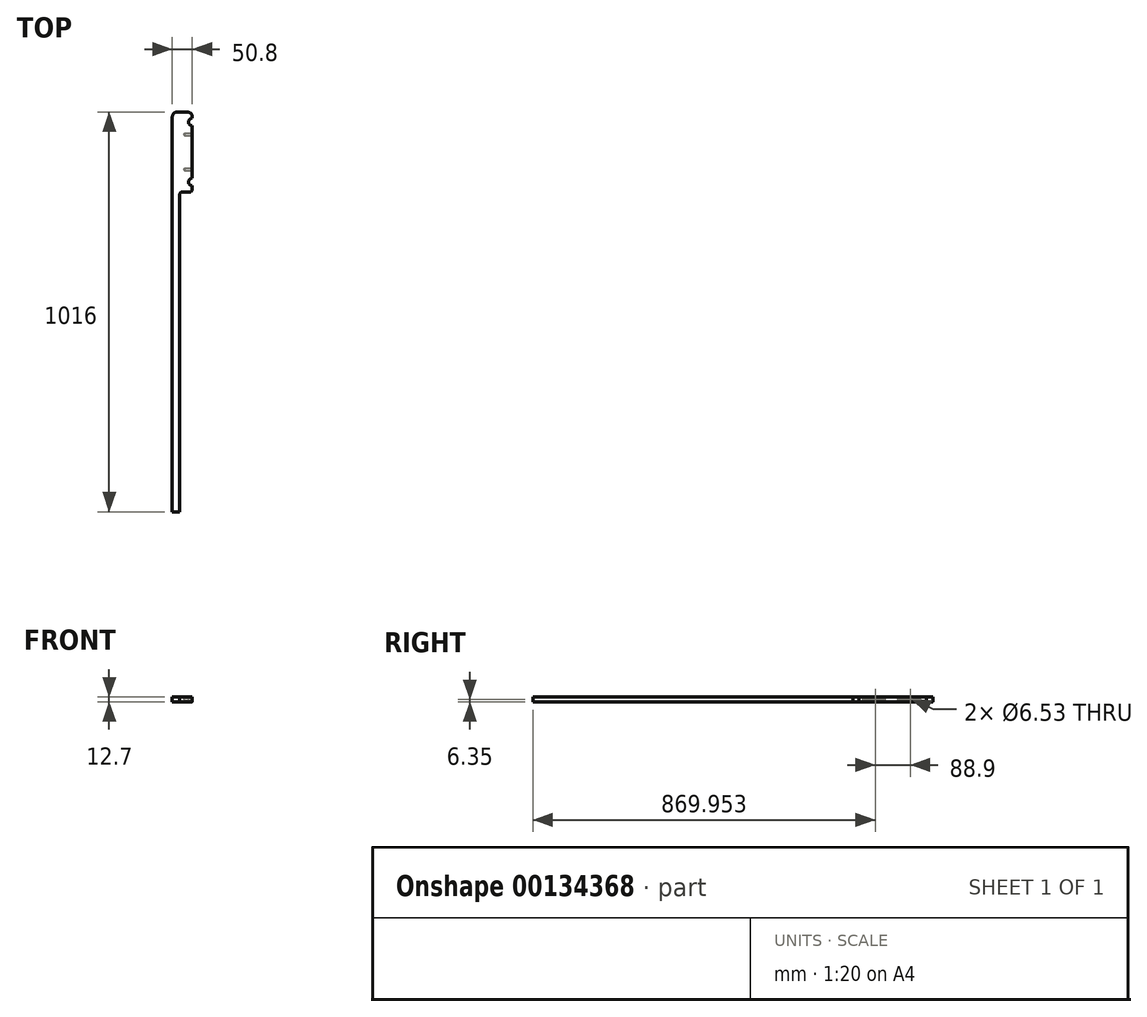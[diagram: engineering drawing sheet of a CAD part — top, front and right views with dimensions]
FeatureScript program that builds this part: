
annotation { "Feature Type Name" : "Feature", "Feature Type Description" : "" }
export const myFeature = defineFeature(function(context is Context, id is Id, definition is map)
    precondition{}
    {
        {
            var Q0;
            Q0=qCreatedBy(makeId("Top.planeOp"),FACE);
            var sketch = newSketch(context, id + "F0", { "sketchPlane" : qUnion([Q0])});
            skLineSegment(sketch, "E0", {"start": v(12.7, 1073.25) * mm, "end": v(38.1, 1073.25) * mm});
            skLineSegment(sketch, "E1", {"start": v(50.8, 1060.55) * mm, "end": v(50.8, 876.4) * mm});
            skLineSegment(sketch, "E2", {"start": v(44.45, 870.05) * mm, "end": v(25.4, 870.05) * mm});
            skLineSegment(sketch, "E3", {"start": v(0, 1060.55) * mm, "end": v(0, 57.25) * mm});
            skLineSegment(sketch, "E4", {"start": v(19.05, 863.7) * mm, "end": v(19.05, 57.25) * mm});
            skLineSegment(sketch, "E5", {"start": v(0, 57.25) * mm, "end": v(19.05, 57.25) * mm});
            skPoint(sketch, "E6.visualSharp", {"position": v(0, 1073.25) * mm});
            skArc(sketch, "E6.filletArc", {"start": v(12.7, 1073.25) * mm, "mid": v(3.72, 1069.53) * mm, "end": v(0, 1060.55) * mm});
            skPoint(sketch, "E7.visualSharp", {"position": v(50.8, 1073.25) * mm});
            skArc(sketch, "E7.filletArc", {"start": v(50.8, 1060.55) * mm, "mid": v(47.08, 1069.53) * mm, "end": v(38.1, 1073.25) * mm});
            skPoint(sketch, "E8.visualSharp", {"position": v(50.8, 870.05) * mm});
            skArc(sketch, "E8.filletArc", {"start": v(44.45, 870.05) * mm, "mid": v(48.94, 871.91) * mm, "end": v(50.8, 876.4) * mm});
            skPoint(sketch, "E9.visualSharp", {"position": v(19.05, 870.05) * mm});
            skArc(sketch, "E9.filletArc", {"start": v(25.4, 870.05) * mm, "mid": v(20.9, 868.2) * mm, "end": v(19.05, 863.7) * mm});
            skSolve(sketch);
        }
        {
            var Q0;
            Q0=makeQuery(id+"F0.imprint","IMPRINT",FACE,{"disambiguationData":[TD([[makeQuery(id+"F0.imprint","IMPRINT",EDGE,{"derivedFrom":sQuery(id+"F0.wireOp",EDGE,"E0")}),-1.0]])]});
            extrude(context, id + "F1", {"entities" : qUnion([Q0]), "depth" : 12.7 * mm});
        }
        {
            var Q0;
            Q0=makeQuery(id+"F1.opExtrude","CAP_FACE",FACE,{"disambiguationData":[OSD([sQuery(id+"F0.wireOp",EDGE,"E0"),sQuery(id+"F0.wireOp",EDGE,"E1"),sQuery(id+"F0.wireOp",EDGE,"E2"),sQuery(id+"F0.wireOp",EDGE,"E3"),sQuery(id+"F0.wireOp",EDGE,"E4"),sQuery(id+"F0.wireOp",EDGE,"E5"),sQuery(id+"F0.wireOp",EDGE,"E6.filletArc"),sQuery(id+"F0.wireOp",EDGE,"E7.filletArc"),sQuery(id+"F0.wireOp",EDGE,"E8.filletArc"),sQuery(id+"F0.wireOp",EDGE,"E9.filletArc")])],"isStart":false});
            var sketch = newSketch(context, id + "F2", { "sketchPlane" : qUnion([Q0])});
            skPoint(sketch, "E10", {"position": v(50.8, 1047.85) * mm});
            skPoint(sketch, "E11", {"position": v(50.8, 895.45) * mm});
            skSolve(sketch);
        }
        {
            var Q0;
            Q0=sQuery(id+"F2.wireOp",VERTEX,"E10");
            var Q1;
            Q1=sQuery(id+"F2.wireOp",VERTEX,"E11");
            var Q2;
            Q2=makeQuery(id+"F1.opExtrude","SWEPT_BODY",BODY,{"disambiguationData":[OSD([sQuery(id+"F0.wireOp",EDGE,"E0"),sQuery(id+"F0.wireOp",EDGE,"E1"),sQuery(id+"F0.wireOp",EDGE,"E2"),sQuery(id+"F0.wireOp",EDGE,"E3"),sQuery(id+"F0.wireOp",EDGE,"E4"),sQuery(id+"F0.wireOp",EDGE,"E5"),sQuery(id+"F0.wireOp",EDGE,"E6.filletArc"),sQuery(id+"F0.wireOp",EDGE,"E7.filletArc"),sQuery(id+"F0.wireOp",EDGE,"E8.filletArc"),sQuery(id+"F0.wireOp",EDGE,"E9.filletArc")])]});
            hole(context, id + "F3", {"style" : HoleStyle.SIMPLE, "endStyle" : HoleEndStyle.THROUGH, "holeDiameter" : 19.05 * mm, "locations" : qUnion([Q0, Q1]), "scope" : qUnion([Q2]), "isTappedThrough" : true});
        }
        {
            var Q0;
            {var subQ1=sQuery(id+"F0.wireOp",EDGE,"E8.filletArc");var subQ8=sQuery(id+"F0.wireOp",EDGE,"E1");var subQ12=makeQuery(id+"F3.hole-0.opRevolve","SWEPT_FACE",FACE,{"disambiguationData":[OSD([sQuery(id+"F3.hole-0.sketch.wireOp",EDGE,"core_line_2")])]});Q0=makeQuery(id+"F3.hole-1.boolean.opBoolean","SPLIT",FACE,{"disambiguationData":[TD([makeQuery(id+"F3.hole-0.boolean.opBoolean","COPY",FACE,{"derivedFrom":subQ12})])],"derivedFrom":makeQuery(id+"F3.hole-0.boolean.opBoolean","SPLIT",FACE,{"disambiguationData":[TD([makeQuery(id+"F1.opExtrude","SWEPT_FACE",FACE,{"disambiguationData":[OSD([subQ1])]})])],"derivedFrom":makeQuery(id+"F1.opExtrude","SWEPT_FACE",FACE,{"disambiguationData":[OSD([subQ8])]})})});}
            var sketch = newSketch(context, id + "F4", { "sketchPlane" : qUnion([Q0])});
            skPoint(sketch, "E12", {"position": v(1016.1, 6.35) * mm});
            skPoint(sketch, "E13", {"position": v(927.2, 6.35) * mm});
            skSolve(sketch);
        }
        {
            var Q0;
            Q0=sQuery(id+"F4.wireOp",VERTEX,"PknFMRSz-I7fV-ZSS9-hOL0-16sDYIYaiRcO.end");
            var Q1;
            Q1=sQuery(id+"F4.wireOp",VERTEX,"E12");
            var Q2;
            Q2=sQuery(id+"F4.wireOp",VERTEX,"E13");
            var Q3;
            Q3=makeQuery(id+"F1.opExtrude","SWEPT_BODY",BODY,{"disambiguationData":[OSD([sQuery(id+"F0.wireOp",EDGE,"E0"),sQuery(id+"F0.wireOp",EDGE,"E1"),sQuery(id+"F0.wireOp",EDGE,"E2"),sQuery(id+"F0.wireOp",EDGE,"E3"),sQuery(id+"F0.wireOp",EDGE,"E4"),sQuery(id+"F0.wireOp",EDGE,"E5"),sQuery(id+"F0.wireOp",EDGE,"E6.filletArc"),sQuery(id+"F0.wireOp",EDGE,"E7.filletArc"),sQuery(id+"F0.wireOp",EDGE,"E8.filletArc"),sQuery(id+"F0.wireOp",EDGE,"E9.filletArc")])]});
            hole(context, id + "F5", {"style" : HoleStyle.SIMPLE, "endStyle" : HoleEndStyle.BLIND, "standardTappedOrClearance" : lookupTablePath({ "standard" : "ANSI", "engagement" : "75%", "pitch" : "18 tpi", "size" : "5/16", "type" : "Tapped" }), "standardBlindInLast" : lookupTablePath({ "standard" : "ANSI", "engagement" : "75%", "pitch" : "18 tpi", "size" : "5/16", "type" : "Tapped" }), "holeDiameter" : 6.53 * mm, "holeDepth" : 19.05 * mm, "locations" : qUnion([Q0, Q1, Q2]), "scope" : qUnion([Q3]), "majorDiameter" : 7.94 * mm});
        }
    });
